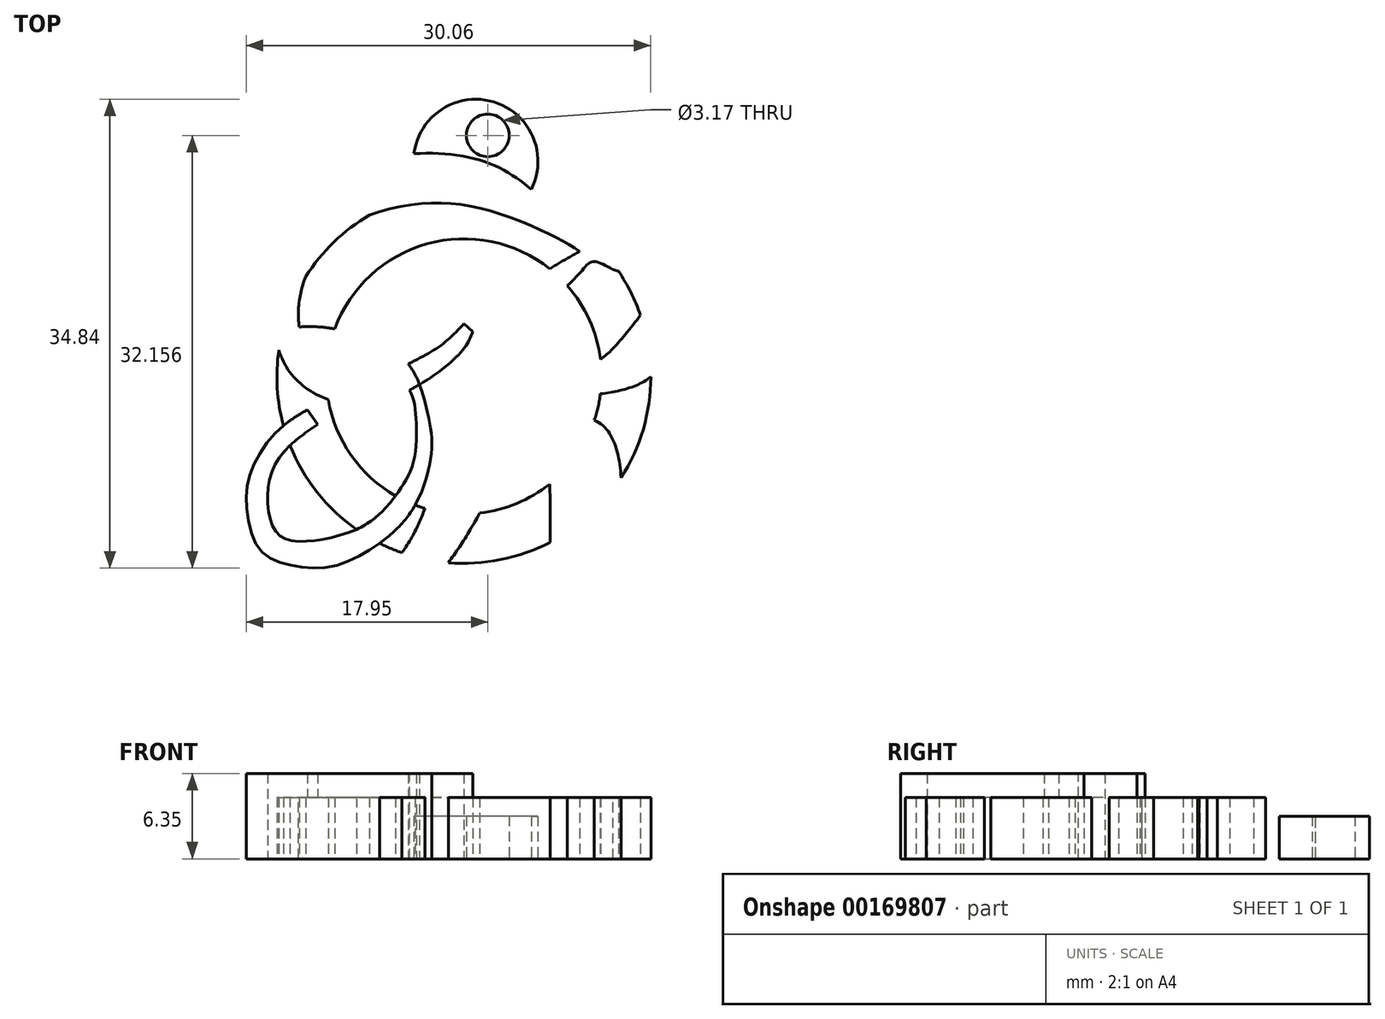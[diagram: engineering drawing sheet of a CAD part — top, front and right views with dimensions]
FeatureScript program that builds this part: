
annotation { "Feature Type Name" : "Feature", "Feature Type Description" : "" }
export const myFeature = defineFeature(function(context is Context, id is Id, definition is map)
    precondition{}
    {
        {
            var Q0;
            Q0=qCreatedBy(makeId("Top.planeOp"),FACE);
            var sketch = newSketch(context, id + "F0", { "sketchPlane" : qUnion([Q0])});
            skFitSpline(sketch, "E0", {"points": [v(6.88, -1.12) * mm, v(3.2, 1.95) * mm, v(-0.89, 4.72) * mm, v(-8.35, 5.2) * mm, v(-14.07, 2.2) * mm, v(-16.72, -2.93) * mm, v(-16.96, -6.72) * mm, v(-15.82, -10.63) * mm, v(-12.15, -13.04) * mm, v(-7.33, -12.38) * mm, v(-3, -9.3) * mm, v(-2.1, -7.8) * mm], "startDerivative": vector(-40.7, 33.48) * mm, "endDerivative": vector(11.05, 25.4) * mm});
            skLineSegment(sketch, "E1", {"start": v(-2.1, -7.8) * mm, "end": v(-2.77, -7.2) * mm});
            skFitSpline(sketch, "E2", {"points": [v(-2.77, -7.2) * mm, v(-4.3, -8.68) * mm, v(-6.42, -9.94) * mm, v(-9.53, -11.16) * mm, v(-13.19, -10.75) * mm, v(-14.94, -7.73) * mm, v(-14.54, -3.76) * mm, v(-11.52, 0) * mm, v(-6.15, 1.7) * mm, v(-1.37, 1.33) * mm, v(3.73, -0.6) * mm, v(5.85, -1.82) * mm], "startDerivative": vector(-21.04, -22.87) * mm, "endDerivative": vector(24.95, -15.7) * mm});
            skFitSpline(sketch, "E3", {"points": [v(5.85, -1.82) * mm, v(2.56, -3.9) * mm, v(-0.51, -7.2) * mm, v(-2.77, -11.11) * mm, v(-3.76, -14.9) * mm, v(-5.2, -19.6) * mm, v(-6.51, -22.84) * mm, v(-8.9, -26.09) * mm, v(-11.43, -28.03) * mm, v(-13.19, -28.52) * mm, v(-16.57, -28.48) * mm, v(-19.64, -27.44) * mm, v(-21.9, -25.46) * mm, v(-24.15, -21.98) * mm, v(-24.1, -16.08) * mm, v(-22.16, -12.38) * mm, v(-18.01, -9.54) * mm, v(-16.61, -8.85) * mm, v(-14.78, -8.43) * mm, v(-12.06, -8.81) * mm, v(-9.04, -9.94) * mm, v(-8.03, -10.7) * mm, v(-6.81, -12.13) * mm, v(-6.33, -14.05) * mm, v(-6.51, -17.43) * mm, v(-7.73, -19.82) * mm, v(-9.98, -22.07) * mm, v(-13.77, -23.3) * mm, v(-16.39, -22.98) * mm, v(-17.34, -20.63) * mm, v(-16.61, -17.34) * mm, v(-13.64, -14.68) * mm], "startDerivative": vector(-95.56, -52.63) * mm, "endDerivative": vector(96.97, 67.05) * mm});
            skLineSegment(sketch, "E4", {"start": v(-13.64, -14.68) * mm, "end": v(-14.4, -13.6) * mm});
            skFitSpline(sketch, "E5", {"points": [v(-14.4, -13.6) * mm, v(-16.52, -15.08) * mm, v(-18.5, -17.97) * mm, v(-18.91, -20.81) * mm, v(-17.97, -23.92) * mm, v(-15.85, -25.1) * mm, v(-12.78, -25.28) * mm, v(-9.71, -23.97) * mm, v(-7.32, -21.98) * mm, v(-5.88, -19.6) * mm, v(-5.16, -16.44) * mm, v(-5.52, -13.6) * mm, v(-6.9, -10.19) * mm, v(-9.8, -8.36) * mm, v(-13.19, -7.46) * mm, v(-16.85, -7.73) * mm, v(-19.6, -8.81) * mm, v(-22.66, -10.8) * mm, v(-24.82, -14.1) * mm, v(-25.68, -18.2) * mm, v(-25.68, -21) * mm, v(-24.91, -23.47) * mm, v(-22.88, -26.58) * mm, v(-20.4, -28.48) * mm, v(-16.8, -29.7) * mm, v(-12.42, -29.65) * mm, v(-7.28, -28.03) * mm, v(-3.13, -23.83) * mm, v(0.48, -16.75) * mm, v(1.02, -14.27) * mm], "startDerivative": vector(-72.63, -42.17) * mm, "endDerivative": vector(9.2, 72.73) * mm});
            skFitSpline(sketch, "E6", {"points": [v(1.02, -14.27) * mm, v(2.51, -14.98) * mm, v(3.55, -18.38) * mm, v(3.64, -23.43) * mm, v(4.04, -26.45) * mm, v(5.3, -28.52) * mm, v(8.1, -29.7) * mm, v(12.39, -29.83) * mm, v(15.45, -28.52) * mm, v(17.62, -26.63) * mm, v(18.97, -23.38) * mm, v(18.34, -19.68) * mm, v(16.22, -17.7) * mm, v(13.47, -17.52) * mm], "startDerivative": vector(29.35, -7.22) * mm, "endDerivative": vector(-39.99, -2.78) * mm});
            skLineSegment(sketch, "E7", {"start": v(13.47, -17.52) * mm, "end": v(13.47, -18.47) * mm});
            skFitSpline(sketch, "E8", {"points": [v(13.47, -18.47) * mm, v(14.91, -18.87) * mm, v(16.63, -20) * mm, v(17.35, -21.67) * mm, v(17.08, -24.01) * mm, v(16.22, -25.46) * mm, v(14.37, -27.26) * mm, v(11.94, -27.8) * mm, v(9.68, -27.08) * mm, v(8.6, -24.74) * mm, v(8.87, -20.72) * mm, v(8.64, -16.8) * mm, v(7.38, -14.63) * mm, v(4.81, -13.91) * mm, v(1.79, -13.41) * mm], "startDerivative": vector(24.24, -5.32) * mm, "endDerivative": vector(-37.55, 6.52) * mm});
            skLineSegment(sketch, "E9", {"start": v(1.79, -13.41) * mm, "end": v(2.1, -12.51) * mm});
            skFitSpline(sketch, "E10", {"points": [v(2.1, -12.51) * mm, v(6.25, -12.51) * mm, v(10.72, -11.43) * mm, v(12.77, -8.74) * mm, v(14.3, -4.63) * mm, v(16.11, -1.48) * mm, v(18.64, 0.96) * mm, v(21.32, 2.15) * mm, v(24.24, 1.91) * mm, v(25.43, 1.53) * mm], "startDerivative": vector(32.22, -1.17) * mm, "endDerivative": vector(15.17, -5.66) * mm});
            skLineSegment(sketch, "E11", {"start": v(25.43, 1.53) * mm, "end": v(25.96, 2.06) * mm});
            skFitSpline(sketch, "E12", {"points": [v(25.96, 2.06) * mm, v(24.43, 2.97) * mm, v(21.56, 3.2) * mm, v(17.88, 2.06) * mm, v(14.92, 0) * mm, v(13.2, -2.96) * mm, v(10.95, -5.83) * mm, v(8.32, -9.03) * mm, v(6.75, -10.27) * mm, v(4.7, -11.18) * mm, v(2.25, -11.37) * mm, v(1.73, -11.37) * mm], "startDerivative": vector(-18.44, 13.8) * mm, "endDerivative": vector(-10.27, 0) * mm});
            skFitSpline(sketch, "E13", {"points": [v(1.73, -11.37) * mm, v(2.03, -10.12) * mm, v(3.12, -6.95) * mm, v(4.06, -5.3) * mm, v(5.91, -3.36) * mm, v(6.8, -2.58) * mm, v(8.3, -3.17) * mm], "startDerivative": vector(1.56, 7.8) * mm, "endDerivative": vector(10.96, -6.4) * mm});
            skFitSpline(sketch, "E14", {"points": [v(8.3, -3.17) * mm, v(9.85, -3.55) * mm, v(11.65, -3.41) * mm, v(12.48, -2.37) * mm, v(12.13, -1.19) * mm, v(11.17, -0.81) * mm, v(9.4, -0.95) * mm, v(7.76, -1.22) * mm, v(7.17, -1.4) * mm, v(6.88, -1.12) * mm], "startDerivative": vector(11.65, -3.45) * mm, "endDerivative": vector(-4.13, 6.01) * mm});
            skFitSpline(sketch, "E15", {"points": [v(9.35, -1.72) * mm, v(8.15, -2) * mm, v(9.4, -2.38) * mm, v(11.3, -2.6) * mm, v(11.67, -2.11) * mm, v(11.55, -1.66) * mm, v(11, -1.57) * mm, v(9.35, -1.72) * mm]});
            skFitSpline(sketch, "E16.trimOffspring", {"points": [v(5.85, -1.82) * mm, v(2.56, -3.9) * mm, v(-0.51, -7.2) * mm, v(-2.77, -11.11) * mm, v(-3.76, -14.9) * mm, v(-5.2, -19.6) * mm, v(-6.51, -22.84) * mm, v(-8.9, -26.09) * mm, v(-11.43, -28.03) * mm, v(-13.19, -28.52) * mm, v(-16.57, -28.48) * mm, v(-19.64, -27.44) * mm, v(-21.9, -25.46) * mm, v(-24.15, -21.98) * mm, v(-24.1, -16.08) * mm, v(-22.16, -12.38) * mm, v(-18.01, -9.54) * mm, v(-16.61, -8.85) * mm, v(-14.78, -8.43) * mm, v(-12.06, -8.81) * mm, v(-9.04, -9.94) * mm, v(-8.03, -10.7) * mm, v(-6.81, -12.13) * mm, v(-6.33, -14.05) * mm, v(-6.51, -17.43) * mm, v(-7.73, -19.82) * mm, v(-9.98, -22.07) * mm, v(-13.77, -23.3) * mm, v(-16.39, -22.98) * mm, v(-17.34, -20.63) * mm, v(-16.61, -17.34) * mm, v(-13.64, -14.68) * mm], "startDerivative": vector(-95.56, -52.63) * mm, "endDerivative": vector(96.97, 67.05) * mm});
            skArc(sketch, "E17", {"start": v(-12.84, -12.84) * mm, "mid": v(-11.15, -16.97) * mm, "end": v(-7.85, -19.98) * mm});
            skArc(sketch, "E18", {"start": v(-9.79, 0.87) * mm, "mid": v(-12.43, -1.14) * mm, "end": v(-14.52, -3.71) * mm});
            skArc(sketch, "E19.trimOffspring", {"start": v(-16.52, -9.17) * mm, "mid": v(-16.63, -11.98) * mm, "end": v(-16.17, -14.77) * mm});
            skArc(sketch, "E20.trimOffspring", {"start": v(-15.68, -16.23) * mm, "mid": v(-13.67, -19.72) * mm, "end": v(-10.75, -22.48) * mm});
            skArc(sketch, "E21.trimOffspring", {"start": v(-9.03, -23.5) * mm, "mid": v(-8.2, -23.9) * mm, "end": v(-7.36, -24.22) * mm});
            skArc(sketch, "E22.trimOffspring", {"start": v(-6.4, -20.67) * mm, "mid": v(-6.03, -20.8) * mm, "end": v(-5.66, -20.92) * mm});
            skArc(sketch, "E23.trimOffspring", {"start": v(-1.6, -21.27) * mm, "mid": v(1.16, -20.56) * mm, "end": v(3.6, -19.11) * mm});
            skArc(sketch, "E24.trimOffspring", {"start": v(-3.92, -24.95) * mm, "mid": v(-0.03, -24.73) * mm, "end": v(3.64, -23.44) * mm});
            skArc(sketch, "E25.trimOffspring", {"start": v(8.9, -18.64) * mm, "mid": v(10.55, -15.05) * mm, "end": v(11.12, -11.14) * mm});
            skArc(sketch, "E26.trimOffspring", {"start": v(6.92, -14.38) * mm, "mid": v(7.2, -13.4) * mm, "end": v(7.37, -12.4) * mm});
            skArc(sketch, "E27.trimOffspring", {"start": v(7.38, -9.85) * mm, "mid": v(6.56, -6.93) * mm, "end": v(4.93, -4.38) * mm});
            skArc(sketch, "E28.trimOffspring", {"start": v(10.36, -6.57) * mm, "mid": v(9.64, -4.88) * mm, "end": v(8.71, -3.3) * mm});
            skArc(sketch, "E29.trimOffspring", {"start": v(7.16, -1.4) * mm, "mid": v(6.23, -0.53) * mm, "end": v(5.22, 0.25) * mm});
            skArc(sketch, "E30.trimOffspring", {"start": v(3.62, -3.13) * mm, "mid": v(-7.09, -1.85) * mm, "end": v(-12.99, -10.87) * mm});
            skCircle(sketch, "E31", {"center": v(-1, 6.8) * mm, "radius": 1.59 * mm});
            skArc(sketch, "E32", {"start": v(2.24, 2.78) * mm, "mid": v(-0.54, 9.28) * mm, "end": v(-6.47, 5.44) * mm});
            skSolve(sketch);
        }
        {
            var Q0;
            {var subQ15=sQuery(id+"F0.wireOp",EDGE,"E1");Q0=makeQuery(id+"F0.imprint","IMPRINT",FACE,{"disambiguationData":[TD([[makeQuery(id+"F0.imprint","IMPRINT",EDGE,{"derivedFrom":subQ15}),1.0]])]});}
            var Q1;
            {var subQ0=sQuery(id+"F0.wireOp",EDGE,"E16.trimOffspring");var subQ1=sQuery(id+"F0.wireOp",EDGE,"E2");var subQ2=makeQuery(id+"F0.imprint","INTERSECT",VERTEX,{"disambiguationData":[OD(1.0)],"derivedFrom":[subQ1,subQ0]});Q1=makeQuery(id+"F0.imprint","IMPRINT",FACE,{"disambiguationData":[TD([[makeQuery(id+"F0.imprint","IMPRINT",EDGE,{"disambiguationData":[TD([[subQ2,1.0]])],"derivedFrom":subQ1}),-1.0]])]});}
            var Q2;
            {var subQ0=sQuery(id+"F0.wireOp",EDGE,"E16.trimOffspring");var subQ1=sQuery(id+"F0.wireOp",EDGE,"E2");var subQ2=makeQuery(id+"F0.imprint","INTERSECT",VERTEX,{"disambiguationData":[OD(0.0)],"derivedFrom":[subQ1,subQ0]});Q2=makeQuery(id+"F0.imprint","IMPRINT",FACE,{"disambiguationData":[TD([[makeQuery(id+"F0.imprint","IMPRINT",EDGE,{"disambiguationData":[TD([[subQ2,-1.0]])],"derivedFrom":subQ1}),-1.0]])]});}
            var Q3;
            {var subQ3=sQuery(id+"F0.wireOp",EDGE,"E4");Q3=makeQuery(id+"F0.imprint","IMPRINT",FACE,{"disambiguationData":[TD([[makeQuery(id+"F0.imprint","IMPRINT",EDGE,{"derivedFrom":subQ3}),1.0]])]});}
            extrude(context, id + "F1", {"entities" : qUnion([Q0, Q1, Q2, Q3]), "depth" : 6.35 * mm});
        }
        {
            var Q0;
            {var subQ5=sQuery(id+"F0.wireOp",EDGE,"E18");Q0=makeQuery(id+"F0.imprint","IMPRINT",FACE,{"disambiguationData":[TD([[makeQuery(id+"F0.imprint","IMPRINT",EDGE,{"derivedFrom":subQ5}),1.0]])]});}
            var Q1;
            {var subQ4=sQuery(id+"F0.wireOp",EDGE,"E4");Q1=makeQuery(id+"F0.imprint","IMPRINT",FACE,{"disambiguationData":[TD([[makeQuery(id+"F0.imprint","IMPRINT",EDGE,{"derivedFrom":subQ4}),-1.0]])]});}
            var Q2;
            {var subQ0=sQuery(id+"F0.wireOp",EDGE,"E16.trimOffspring");var subQ1=sQuery(id+"F0.wireOp",EDGE,"E2");var subQ2=makeQuery(id+"F0.imprint","INTERSECT",VERTEX,{"disambiguationData":[OD(0.0)],"derivedFrom":[subQ1,subQ0]});Q2=makeQuery(id+"F0.imprint","IMPRINT",FACE,{"disambiguationData":[TD([[makeQuery(id+"F0.imprint","IMPRINT",EDGE,{"disambiguationData":[TD([[subQ2,1.0]])],"derivedFrom":subQ1}),-1.0]])]});}
            var Q3;
            {var subQ0=sQuery(id+"F0.wireOp",EDGE,"E23.trimOffspring");Q3=makeQuery(id+"F0.imprint","IMPRINT",FACE,{"disambiguationData":[TD([[makeQuery(id+"F0.imprint","IMPRINT",EDGE,{"derivedFrom":subQ0}),-1.0]])]});}
            var Q4;
            {var subQ0=sQuery(id+"F0.wireOp",EDGE,"E21.trimOffspring");Q4=makeQuery(id+"F0.imprint","IMPRINT",FACE,{"disambiguationData":[TD([[makeQuery(id+"F0.imprint","IMPRINT",EDGE,{"derivedFrom":subQ0}),1.0]])]});}
            var Q5;
            {var subQ0=sQuery(id+"F0.wireOp",EDGE,"E25.trimOffspring");Q5=makeQuery(id+"F0.imprint","IMPRINT",FACE,{"disambiguationData":[TD([[makeQuery(id+"F0.imprint","IMPRINT",EDGE,{"derivedFrom":subQ0}),1.0]])]});}
            var Q6;
            {var subQ0=sQuery(id+"F0.wireOp",EDGE,"E27.trimOffspring");Q6=makeQuery(id+"F0.imprint","IMPRINT",FACE,{"disambiguationData":[TD([[makeQuery(id+"F0.imprint","IMPRINT",EDGE,{"derivedFrom":subQ0}),-1.0]])]});}
            extrude(context, id + "F2", {"entities" : qUnion([Q0, Q1, Q2, Q3, Q4, Q5, Q6]), "operationType" : NewBodyOperationType.ADD, "depth" : 4.57 * mm});
        }
        {
            var Q0;
            Q0=makeQuery(id+"F0.imprint","IMPRINT",FACE,{"disambiguationData":[TD([[makeQuery(id+"F0.imprint","IMPRINT",EDGE,{"derivedFrom":sQuery(id+"F0.wireOp",EDGE,"E31")}),-1.0]])]});
            extrude(context, id + "F3", {"entities" : qUnion([Q0]), "operationType" : NewBodyOperationType.ADD, "depth" : 3.17 * mm});
        }
    });
